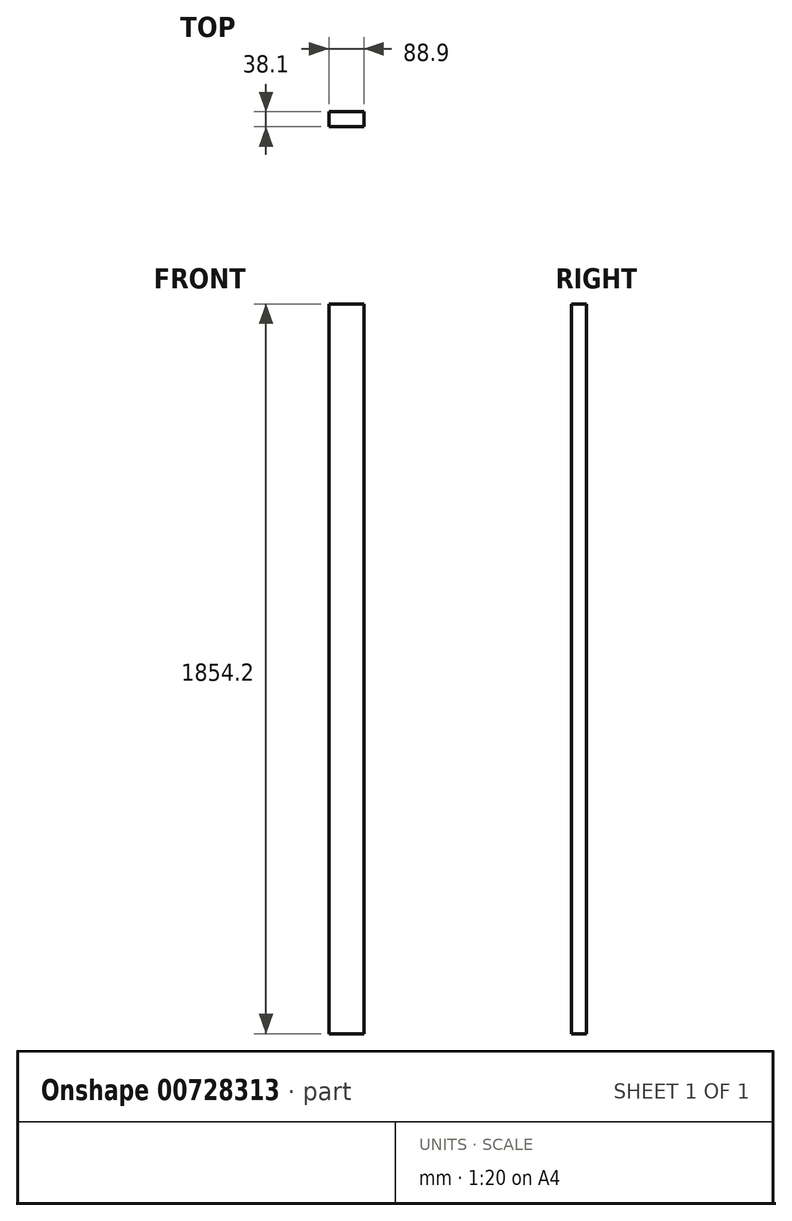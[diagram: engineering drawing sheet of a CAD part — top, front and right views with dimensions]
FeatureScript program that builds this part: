
annotation { "Feature Type Name" : "Feature", "Feature Type Description" : "" }
export const myFeature = defineFeature(function(context is Context, id is Id, definition is map)
    precondition{}
    {
        {
            var Q0;
            Q0=qCreatedBy(makeId("Front.planeOp"),FACE);
            var sketch = newSketch(context, id + "F0", { "sketchPlane" : qUnion([Q0])});
            skLineSegment(sketch, "E0.bottom", {"start": v(-44.45, -927.1) * mm, "end": v(44.45, -927.1) * mm});
            skLineSegment(sketch, "E0.top", {"start": v(-44.45, 927.1) * mm, "end": v(44.45, 927.1) * mm});
            skLineSegment(sketch, "E0.left", {"start": v(-44.45, -927.1) * mm, "end": v(-44.45, 927.1) * mm});
            skLineSegment(sketch, "E0.right", {"start": v(44.45, -927.1) * mm, "end": v(44.45, 927.1) * mm});
            skPoint(sketch, "E0.middle", {"position": v(0, 0) * mm});
            skSolve(sketch);
        }
        {
            var Q0;
            Q0=qSketchRegion(id+"F0",true);
            extrude(context, id + "F1", {"entities" : qUnion([Q0]), "depth" : 38.1 * mm});
        }
    });
